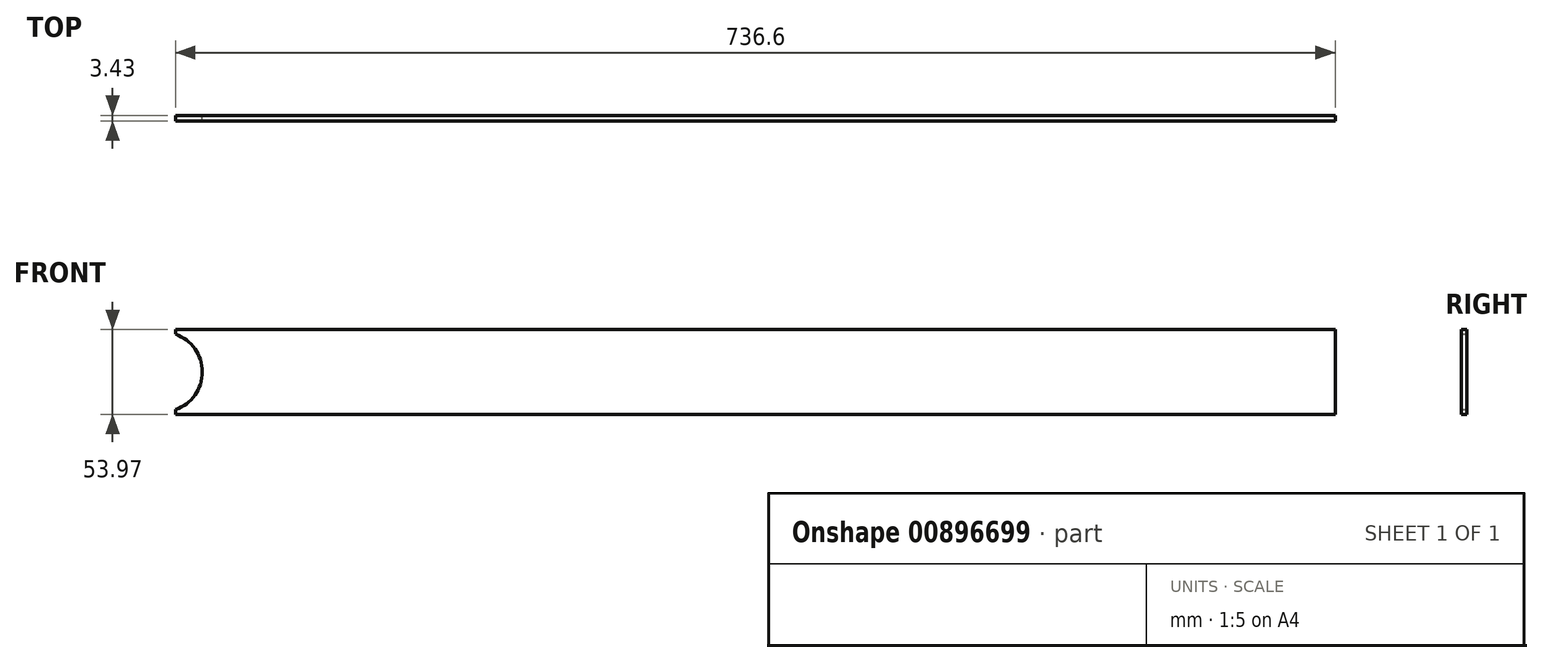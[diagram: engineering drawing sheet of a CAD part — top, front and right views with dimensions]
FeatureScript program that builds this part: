
annotation { "Feature Type Name" : "Feature", "Feature Type Description" : "" }
export const myFeature = defineFeature(function(context is Context, id is Id, definition is map)
    precondition{}
    {
        {
            var Q0;
            Q0=qCreatedBy(makeId("Front.planeOp"),FACE);
            var sketch = newSketch(context, id + "F0", { "sketchPlane" : qUnion([Q0])});
            skLineSegment(sketch, "E0", {"start": v(882.42, 509.95) * mm, "end": v(145.82, 509.95) * mm});
            skLineSegment(sketch, "E1", {"start": v(882.42, 455.98) * mm, "end": v(882.42, 509.95) * mm});
            skLineSegment(sketch, "E2", {"start": v(145.82, 455.98) * mm, "end": v(882.42, 455.98) * mm});
            skLineSegment(sketch, "E3", {"start": v(145.82, 458.99) * mm, "end": v(145.82, 455.98) * mm});
            skArc(sketch, "E4", {"start": v(145.82, 458.99) * mm, "mid": v(162.84, 482.96) * mm, "end": v(145.82, 506.94) * mm});
            skLineSegment(sketch, "E5", {"start": v(145.82, 509.95) * mm, "end": v(145.82, 506.94) * mm});
            skSolve(sketch);
        }
        {
            var Q0;
            Q0 = qSketchRegion(id + "F0", true);
            extrude(context, id + "F1", {"entities" : qUnion([Q0]), "depth" : 3.43 * mm, "offsetDistance" : 25.4 * mm});
        }
    });
